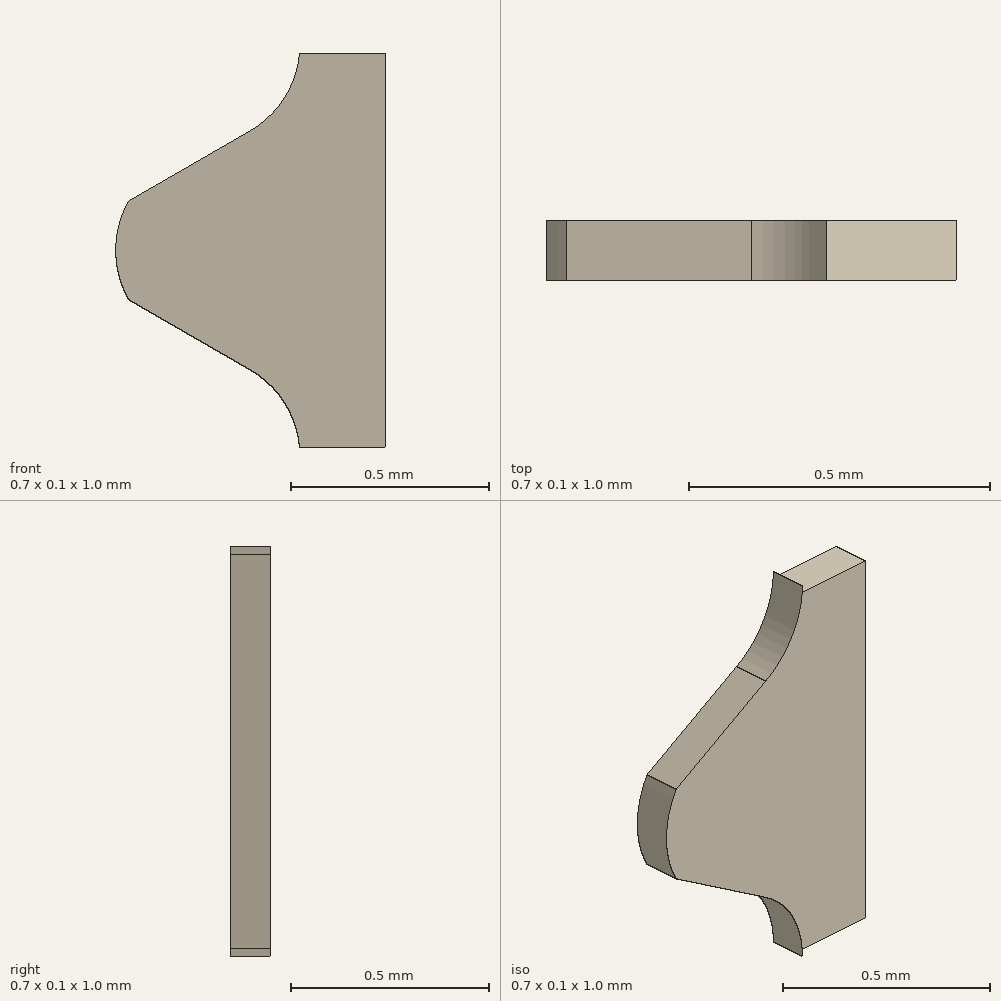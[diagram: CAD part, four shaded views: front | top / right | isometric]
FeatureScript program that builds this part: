
annotation { "Feature Type Name" : "Feature", "Feature Type Description" : "" }
export const myFeature = defineFeature(function(context is Context, id is Id, definition is map)
    precondition{}
    {
        {
            var Q0;
            Q0=qCreatedBy(makeId("Front.planeOp"),FACE);
            var sketch = newSketch(context, id + "F0", { "sketchPlane" : qUnion([Q0]), "disableImprinting" : false});
            skLineSegment(sketch, "E0", {"start": v(0, 0) * mm, "end": v(0.22, 0.12) * mm, "construction": true});
            skLineSegment(sketch, "E1", {"start": v(0, 0) * mm, "end": v(0.22, -0.12) * mm, "construction": true});
            skLineSegment(sketch, "E2", {"start": v(0, 0) * mm, "end": v(0.87, 0) * mm, "construction": true});
            skLineSegment(sketch, "E3", {"start": v(0.87, 0.5) * mm, "end": v(0.87, -0.5) * mm});
            skLineSegment(sketch, "E4", {"start": v(0.43, 0.25) * mm, "end": v(0.43, -0.25) * mm, "construction": true});
            skLineSegment(sketch, "E5", {"start": v(0.22, 0.13) * mm, "end": v(0.22, -0.12) * mm, "construction": true});
            skArc(sketch, "E6", {"start": v(0.22, -0.13) * mm, "mid": v(0.18, 0) * mm, "end": v(0.22, 0.13) * mm});
            skLineSegment(sketch, "E7", {"start": v(0.22, -0.12) * mm, "end": v(0.52, -0.3) * mm});
            skLineSegment(sketch, "E8", {"start": v(0.22, 0.12) * mm, "end": v(0.52, 0.3) * mm});
            skLineSegment(sketch, "E9", {"start": v(0.87, -0.5) * mm, "end": v(0.65, -0.5) * mm});
            skLineSegment(sketch, "E10", {"start": v(0.87, 0.5) * mm, "end": v(0.65, 0.5) * mm});
            skLineSegment(sketch, "E11", {"start": v(0.65, 0.52) * mm, "end": v(0.65, 0.5) * mm});
            skLineSegment(sketch, "E12", {"start": v(0.65, 0.38) * mm, "end": v(0.65, -0.38) * mm, "construction": true});
            skLineSegment(sketch, "E13", {"start": v(0.65, -0.5) * mm, "end": v(0.65, -0.52) * mm});
            skLineSegment(sketch, "E14", {"start": v(0.65, 0.38) * mm, "end": v(0.87, 0.5) * mm, "construction": true});
            skLineSegment(sketch, "E15", {"start": v(0.65, -0.37) * mm, "end": v(0.87, -0.5) * mm, "construction": true});
            skPoint(sketch, "E16.visualSharp", {"position": v(0.65, 0.38) * mm});
            skArc(sketch, "E16.filletArc", {"start": v(0.52, 0.3) * mm, "mid": v(0.62, 0.4) * mm, "end": v(0.65, 0.52) * mm});
            skPoint(sketch, "E17.visualSharp", {"position": v(0.65, -0.38) * mm});
            skArc(sketch, "E17.filletArc", {"start": v(0.65, -0.52) * mm, "mid": v(0.62, -0.4) * mm, "end": v(0.52, -0.3) * mm});
            skLineSegment(sketch, "E18", {"start": v(0.52, 0.3) * mm, "end": v(0.65, 0.37) * mm, "construction": true});
            skLineSegment(sketch, "E19", {"start": v(0.52, -0.3) * mm, "end": v(0.65, -0.37) * mm, "construction": true});
            skSolve(sketch);
        }
        {
            var Q0;
            Q0=makeQuery(id+"F0.imprint","IMPRINT",FACE,{"disambiguationData":[TD([[makeQuery(id+"F0.imprint","IMPRINT",EDGE,{"derivedFrom":sQuery(id+"F0.wireOp",EDGE,"E3")}),-1.0]])]});
            extrude(context, id + "F1", {"entities" : qUnion([Q0]), "depth" : .1 * mm});
        }
    });
